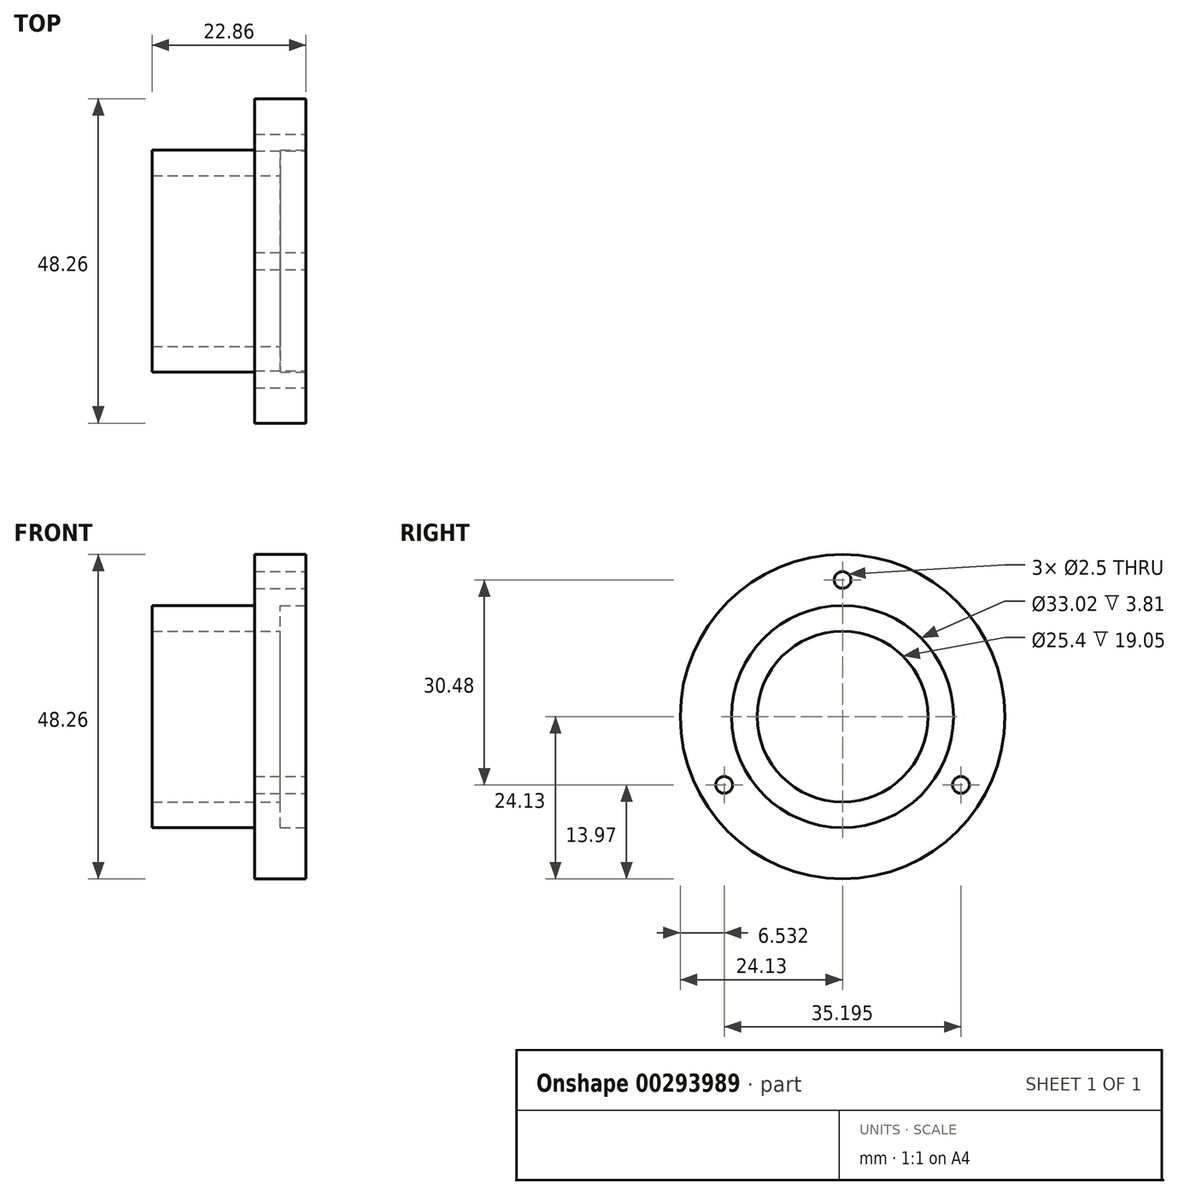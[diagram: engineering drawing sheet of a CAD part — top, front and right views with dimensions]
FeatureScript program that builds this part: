
annotation { "Feature Type Name" : "Feature", "Feature Type Description" : "" }
export const myFeature = defineFeature(function(context is Context, id is Id, definition is map)
    precondition{}
    {
        {
            var Q0;
            Q0=qCreatedBy(makeId("Right.planeOp"),FACE);
            var sketch = newSketch(context, id + "F0", { "sketchPlane" : qUnion([Q0])});
            skCircle(sketch, "E0", {"center": v(0, 0) * mm, "radius": 24.13 * mm});
            skSolve(sketch);
        }
        {
            var Q0;
            Q0=makeQuery(id+"F0.imprint","IMPRINT",FACE,{"disambiguationData":[TD([[makeQuery(id+"F0.imprint","IMPRINT",EDGE,{"derivedFrom":sQuery(id+"F0.wireOp",EDGE,"E0")}),1.0]])]});
            extrude(context, id + "F1", {"entities" : qUnion([Q0]), "depth" : 22.86 * mm});
        }
        {
            var Q0;
            Q0=makeQuery(id+"F1.opExtrude","CAP_FACE",FACE,{"disambiguationData":[OSD([sQuery(id+"F0.wireOp",EDGE,"E0")])],"isStart":false});
            var sketch = newSketch(context, id + "F2", { "sketchPlane" : qUnion([Q0])});
            skCircle(sketch, "E1", {"center": v(0, 0) * mm, "radius": 16.51 * mm});
            skSolve(sketch);
        }
        {
            var Q0;
            Q0=makeQuery(id+"F2.imprint","IMPRINT",FACE,{"disambiguationData":[TD([[makeQuery(id+"F2.imprint","IMPRINT",EDGE,{"derivedFrom":sQuery(id+"F2.wireOp",EDGE,"E1")}),1.0]])]});
            extrude(context, id + "F3", {"entities" : qUnion([Q0]), "operationType" : NewBodyOperationType.REMOVE, "oppositeDirection" : true, "depth" : 3.8 * mm});
        }
        {
            var Q0;
            Q0=makeQuery(id+"F3.boolean.opBoolean","COPY",FACE,{"derivedFrom":makeQuery(id+"F3.opExtrude","CAP_FACE",FACE,{"disambiguationData":[OSD([sQuery(id+"F2.wireOp",EDGE,"E1")])],"isStart":false})});
            var sketch = newSketch(context, id + "F4", { "sketchPlane" : qUnion([Q0])});
            skCircle(sketch, "E2", {"center": v(0, 0) * mm, "radius": 12.7 * mm});
            skSolve(sketch);
        }
        {
            var Q0;
            Q0=makeQuery(id+"F4.imprint","IMPRINT",FACE,{"disambiguationData":[TD([[makeQuery(id+"F4.imprint","IMPRINT",EDGE,{"derivedFrom":sQuery(id+"F4.wireOp",EDGE,"E2")}),1.0]])]});
            var Q1;
            Q1=makeQuery(id+"F1.opExtrude","CAP_FACE",FACE,{"disambiguationData":[OSD([sQuery(id+"F0.wireOp",EDGE,"E0")])],"isStart":true});
            extrude(context, id + "F5", {"entities" : qUnion([Q0]), "operationType" : NewBodyOperationType.REMOVE, "endBound" : BoundingType.UP_TO_SURFACE, "oppositeDirection" : true, "endBoundEntityFace" : qUnion([Q1]), "depth" : 25.4 * mm});
        }
        {
            var Q0;
            Q0=makeQuery(id+"F1.opExtrude","CAP_FACE",FACE,{"disambiguationData":[OSD([sQuery(id+"F0.wireOp",EDGE,"E0")])],"isStart":true});
            var sketch = newSketch(context, id + "F6", { "sketchPlane" : qUnion([Q0])});
            skCircle(sketch, "E3", {"center": v(0, 0) * mm, "radius": 16.51 * mm});
            skSolve(sketch);
        }
        {
            var Q0;
            Q0=makeQuery(id+"F6.imprint","IMPRINT",FACE,{"disambiguationData":[TD([[makeQuery(id+"F6.imprint","IMPRINT",EDGE,{"derivedFrom":sQuery(id+"F6.wireOp",EDGE,"E3")}),-1.0]])]});
            extrude(context, id + "F7", {"entities" : qUnion([Q0]), "operationType" : NewBodyOperationType.REMOVE, "oppositeDirection" : true, "depth" : 15.24 * mm});
        }
        {
            var Q0;
            Q0=makeQuery(id+"F1.opExtrude","CAP_FACE",FACE,{"disambiguationData":[OSD([sQuery(id+"F0.wireOp",EDGE,"E0")])],"isStart":false});
            var sketch = newSketch(context, id + "F8", { "sketchPlane" : qUnion([Q0])});
            skLineSegment(sketch, "E4", {"start": v(0, 0) * mm, "end": v(0, 20.32) * mm, "construction": true});
            skLineSegment(sketch, "E5", {"start": v(0, 20.32) * mm, "end": v(0, 0) * mm, "construction": true});
            skLineSegment(sketch, "E6", {"start": v(0, 0) * mm, "end": v(-17.6, -10.16) * mm, "construction": true});
            skLineSegment(sketch, "E7", {"start": v(-17.6, -10.16) * mm, "end": v(0, 0) * mm, "construction": true});
            skLineSegment(sketch, "E8", {"start": v(0, 0) * mm, "end": v(17.6, -10.16) * mm, "construction": true});
            skCircle(sketch, "E9", {"center": v(0, 20.32) * mm, "radius": 1.25 * mm});
            skCircle(sketch, "E10", {"center": v(-17.6, -10.16) * mm, "radius": 1.25 * mm});
            skCircle(sketch, "E11", {"center": v(17.6, -10.16) * mm, "radius": 1.25 * mm});
            skSolve(sketch);
        }
        {
            var Q0;
            Q0 = qSketchRegion(id + "F8", true);
            var Q1;
            Q1=makeQuery(id+"F7.boolean.opBoolean","COPY",FACE,{"derivedFrom":makeQuery(id+"F7.opExtrude","CAP_FACE",FACE,{"disambiguationData":[OSD([sQuery(id+"F0.wireOp",EDGE,"E0"),sQuery(id+"F6.wireOp",EDGE,"E3")])],"isStart":false})});
            extrude(context, id + "F9", {"entities" : qUnion([Q0, Q1]), "operationType" : NewBodyOperationType.REMOVE, "oppositeDirection" : true, "depth" : 25.4 * mm});
        }
    });
